FCSTD DOCUMENT  (FreeCAD 0.18.3R)
Label: MobileHolder
License: All rights reserved
LicenseURL: http://en.wikipedia.org/wiki/All_rights_reserved
objects: Sketcher::SketchObject×1, PartDesign::Body×1, App::Part×1
note: 2 computed .brp shape members not serialized (recipe doc carries the construction recipe); baked Part::Feature solids carry a one-line shape summary decoded from their .brp

FEATURE [Sketcher::SketchObject] Sketch
  MapMode = 5
  Support = -> [XY_Plane001]
  sketch-geometry (32):
    g0: LineSegment StartX=-12.5 StartY=22.5 StartZ=0 EndX=12.5 EndY=22.5 EndZ=0
    g1: LineSegment StartX=16.5 StartY=18.5 StartZ=0 EndX=16.5 EndY=-18.5 EndZ=0
    g2: LineSegment StartX=12.5 StartY=-22.5 StartZ=0 EndX=-12.5 EndY=-22.5 EndZ=0
    g3: LineSegment StartX=-16.5 StartY=-18.5 StartZ=0 EndX=-16.5 EndY=18.5 EndZ=0
    g4: LineSegment [constr] StartX=-16.5 StartY=0 StartZ=0 EndX=16.5 EndY=0 EndZ=0
    g5: LineSegment [constr] StartX=1e-16 StartY=22.5 StartZ=0 EndX=1e-16 EndY=-22.5 EndZ=0
    g6: LineSegment StartX=-11.5 StartY=17.8 StartZ=0 EndX=-5.5 EndY=17.8 EndZ=0
    g7: LineSegment StartX=-5.5 StartY=17.8 StartZ=0 EndX=-5.5 EndY=12.3 EndZ=0
    g8: LineSegment StartX=-5.5 StartY=12.3 StartZ=0 EndX=-11.5 EndY=12.3 EndZ=0
    g9: LineSegment StartX=-11.5 StartY=12.3 StartZ=0 EndX=-11.5 EndY=17.8 EndZ=0
    g10: LineSegment StartX=5.5 StartY=17.8 StartZ=0 EndX=11.5 EndY=17.8 EndZ=0
    g11: LineSegment StartX=11.5 StartY=17.8 StartZ=0 EndX=11.5 EndY=12.3 EndZ=0
    g12: LineSegment StartX=11.5 StartY=12.3 StartZ=0 EndX=5.5 EndY=12.3 EndZ=0
    g13: LineSegment StartX=5.5 StartY=12.3 StartZ=0 EndX=5.5 EndY=17.8 EndZ=0
    g14: LineSegment StartX=-11.5 StartY=-12.3 StartZ=0 EndX=-5.5 EndY=-12.3 EndZ=0
    g15: LineSegment StartX=-5.5 StartY=-12.3 StartZ=0 EndX=-5.5 EndY=-17.8 EndZ=0
    g16: LineSegment StartX=-5.5 StartY=-17.8 StartZ=0 EndX=-11.5 EndY=-17.8 EndZ=0
    g17: LineSegment StartX=-11.5 StartY=-17.8 StartZ=0 EndX=-11.5 EndY=-12.3 EndZ=0
    g18: LineSegment StartX=5.5 StartY=-12.3 StartZ=0 EndX=11.5 EndY=-12.3 EndZ=0
    g19: LineSegment StartX=11.5 StartY=-12.3 StartZ=0 EndX=11.5 EndY=-17.8 EndZ=0
    g20: LineSegment StartX=11.5 StartY=-17.8 StartZ=0 EndX=5.5 EndY=-17.8 EndZ=0
    g21: LineSegment StartX=5.5 StartY=-17.8 StartZ=0 EndX=5.5 EndY=-12.3 EndZ=0
    g22: LineSegment [constr] StartX=-5.5 StartY=-12.3 StartZ=0 EndX=5.5 EndY=-12.3 EndZ=0
    g23: LineSegment [constr] StartX=5.5 StartY=-12.3 StartZ=0 EndX=5.5 EndY=12.3 EndZ=0
    g24: LineSegment [constr] StartX=5.5 StartY=12.3 StartZ=0 EndX=-5.5 EndY=12.3 EndZ=0
    g25: LineSegment [constr] StartX=-5.5 StartY=12.3 StartZ=0 EndX=-5.5 EndY=-12.3 EndZ=0
    g26: LineSegment [constr] StartX=-8.5 StartY=17.8 StartZ=0 EndX=-8.5 EndY=12.3 EndZ=0
    g27: GeomPoint X=0 Y=0 Z=0
    g28: ArcOfCircle CenterX=12.5 CenterY=-18.5 CenterZ=0 NormalX=0 NormalY=0 NormalZ=1 AngleXU=0 Radius=4 StartAngle=4.71239 EndAngle=6.28319
    g29: ArcOfCircle CenterX=-12.5 CenterY=-18.5 CenterZ=0 NormalX=0 NormalY=0 NormalZ=1 AngleXU=0 Radius=4 StartAngle=3.14159 EndAngle=4.71239
    g30: ArcOfCircle CenterX=-12.5 CenterY=18.5 CenterZ=0 NormalX=0 NormalY=0 NormalZ=1 AngleXU=0 Radius=4 StartAngle=1.5708 EndAngle=3.14159
    g31: ArcOfCircle CenterX=12.5 CenterY=18.5 CenterZ=0 NormalX=0 NormalY=0 NormalZ=1 AngleXU=0 Radius=4 StartAngle=0 EndAngle=1.5708
  constraints (85):
    c: Horizontal(g0)
    c: Horizontal(g2)
    c: Vertical(g1)
    c: Vertical(g3)
    c: PointOnObject(g4,g3)
    c: PointOnObject(g4,g1)
    c: PointOnObject(g5,g0)
    c: PointOnObject(g5,g2)
    c: Coincident(g6,g7)
    c: Coincident(g7,g8)
    c: Coincident(g8,g9)
    c: Coincident(g9,g6)
    c: Horizontal(g6)
    c: Horizontal(g8)
    c: Vertical(g7)
    c: Vertical(g9)
    c: Coincident(g10,g11)
    c: Coincident(g11,g12)
    c: Coincident(g12,g13)
    c: Coincident(g13,g10)
    c: Horizontal(g10)
    c: Horizontal(g12)
    c: Vertical(g11)
    c: Vertical(g13)
    c: Coincident(g14,g15)
    c: Coincident(g15,g16)
    c: Coincident(g16,g17)
    c: Coincident(g17,g14)
    c: Horizontal(g14)
    c: Horizontal(g16)
    c: Vertical(g15)
    c: Vertical(g17)
    c: Coincident(g18,g19)
    c: Coincident(g19,g20)
    c: Coincident(g20,g21)
    c: Coincident(g21,g18)
    c: Horizontal(g18)
    c: Horizontal(g20)
    c: Vertical(g19)
    c: Vertical(g21)
    c: Coincident(g22,g14)
    c: Coincident(g22,g18)
    c: Coincident(g23,g18)
    c: Coincident(g23,g12)
    c: Coincident(g24,g12)
    c: Coincident(g24,g7)
    c: Vertical(g23)
    c: Equal(g9,g13)
    c: Equal(g13,g21)
    c: Equal(g21,g17)
    c: Equal(g6,g10)
    c: Equal(g10,g18)
    c: Equal(g18,g14)
    c: Coincident(g25,g7)
    c: Coincident(g25,g14)
    c: Symmetric(g7,g12,g5)
    c: Symmetric(g7,g14,g4)
    c: Horizontal(g22)
    c: DistanceX(g6,g6) = 6
    c: DistanceY(g9,g9) = 5.5
    c: DistanceY(g16,g6) = 35.6
    c: DistanceX(g6,g10) = 23
    c: PointOnObject(g26,g6)
    c: PointOnObject(g26,g8)
    c: Vertical(g26)
    c: DistanceX(g6,g26) = 3
    c: PointOnObject(g27,g5)
    c: PointOnObject(g27,g4)
    c: Coincident(g27,g-1)  '__ANCHOR__'
    c: Tangent(g1,g28) = 1.5708
    c: Tangent(g2,g28) = 1.5708
    c: Radius(g28) = 4
    c: Tangent(g2,g29) = 1.5708
    c: Tangent(g3,g29) = 1.5708
    c: Equal(g29,g28)
    c: Tangent(g0,g30) = 1.5708
    c: Tangent(g3,g30) = 1.5708
    c: Equal(g30,g29)
    c: DistanceY(g2,g0) = 45
    c: Tangent(g0,g31) = 1.5708
    c: Tangent(g1,g31) = 1.5708
    c: Equal(g31,g30)
    c: DistanceX(g3,g1) = 33
    c: Symmetric(g3,g3,g4)
    c: Symmetric(g0,g0,g5)
FEATURE [PartDesign::Body] Body
  Group = -> [Sketch]
  Origin = -> Origin001
FEATURE [App::Part] Part
  Group = -> [Body]
  Origin = -> Origin
